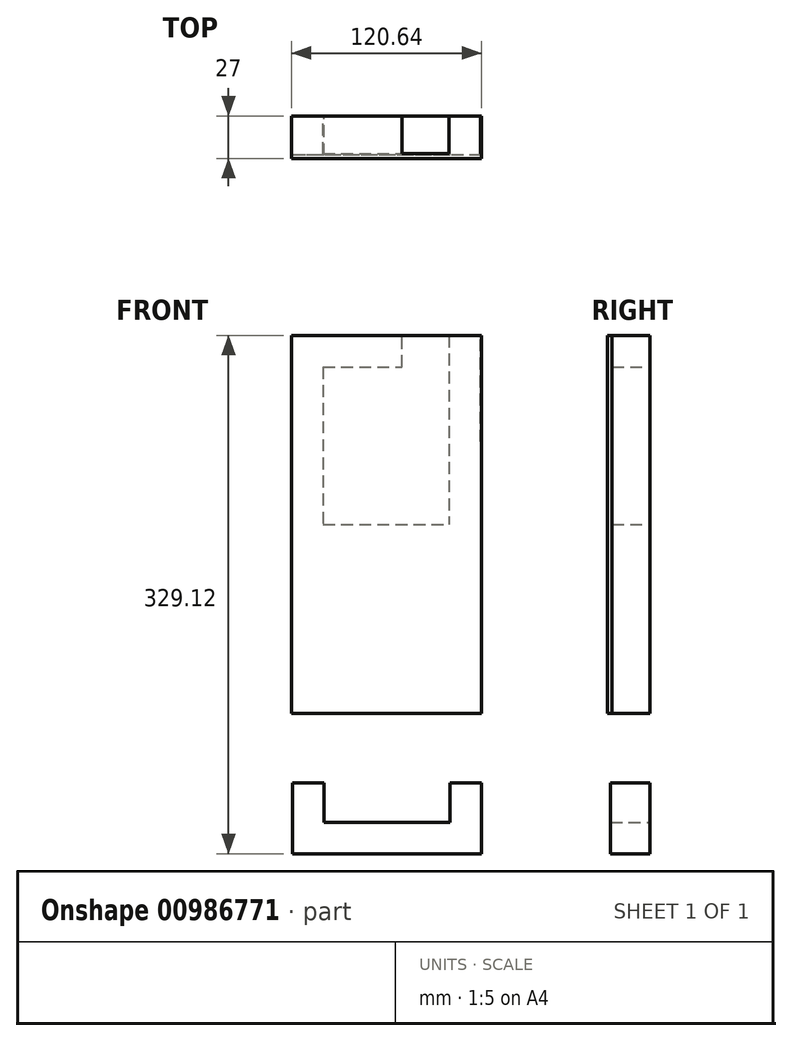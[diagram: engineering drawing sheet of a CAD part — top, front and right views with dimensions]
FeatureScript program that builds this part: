
annotation { "Feature Type Name" : "Feature", "Feature Type Description" : "" }
export const myFeature = defineFeature(function(context is Context, id is Id, definition is map)
    precondition{}
    {
        {
            var Q0;
            Q0=qCreatedBy(makeId("Front.planeOp"),FACE);
            var sketch = newSketch(context, id + "F0", { "sketchPlane" : qUnion([Q0])});
            skLineSegment(sketch, "E0.bottom", {"start": v(0, 0) * mm, "end": v(120, 0) * mm});
            skLineSegment(sketch, "E0.top", {"start": v(-0.64, 240) * mm, "end": v(119.36, 240) * mm});
            skLineSegment(sketch, "E0.left", {"start": v(0, 0) * mm, "end": v(-0.64, 240) * mm});
            skLineSegment(sketch, "E0.right", {"start": v(120, 0) * mm, "end": v(119.36, 240) * mm});
            skLineSegment(sketch, "E1.bottom", {"start": v(19.41, 220) * mm, "end": v(99.41, 220) * mm});
            skLineSegment(sketch, "E1.top", {"start": v(19.41, 40) * mm, "end": v(99.41, 40) * mm});
            skLineSegment(sketch, "E1.left", {"start": v(19.41, 200) * mm, "end": v(19.41, 40) * mm});
            skLineSegment(sketch, "E1.right", {"start": v(99.41, 220) * mm, "end": v(99.41, 40) * mm});
            skLineSegment(sketch, "E2.bottom", {"start": v(19.41, 120) * mm, "end": v(99.41, 120) * mm});
            skLineSegment(sketch, "E2.left", {"start": v(19.41, 120) * mm, "end": v(19.41, 220) * mm});
            skLineSegment(sketch, "E2.right", {"start": v(99.41, 120) * mm, "end": v(99.41, 130) * mm});
            skLineSegment(sketch, "E3", {"start": v(19.41, 220) * mm, "end": v(19.36, 240) * mm});
            skLineSegment(sketch, "E4", {"start": v(19.36, 240) * mm, "end": v(69.41, 240) * mm});
            skLineSegment(sketch, "E5", {"start": v(69.41, 240) * mm, "end": v(69.41, 220) * mm});
            skLineSegment(sketch, "E6", {"start": v(69.41, 220) * mm, "end": v(19.41, 220) * mm});
            skLineSegment(sketch, "E7.bottom", {"start": v(120, -44.12) * mm, "end": v(0, -44.12) * mm});
            skLineSegment(sketch, "E7.top", {"start": v(120, -89.12) * mm, "end": v(0, -89.12) * mm});
            skLineSegment(sketch, "E7.left", {"start": v(120, -44.12) * mm, "end": v(120, -89.12) * mm});
            skLineSegment(sketch, "E7.right", {"start": v(0, -44.12) * mm, "end": v(0, -89.12) * mm});
            skLineSegment(sketch, "E8.bottom", {"start": v(99.9, -44.12) * mm, "end": v(19.9, -44.12) * mm});
            skLineSegment(sketch, "E8.top", {"start": v(99.9, -69.12) * mm, "end": v(19.9, -69.12) * mm});
            skLineSegment(sketch, "E8.left", {"start": v(99.9, -44.12) * mm, "end": v(99.9, -69.12) * mm});
            skLineSegment(sketch, "E8.right", {"start": v(19.9, -44.12) * mm, "end": v(19.9, -69.12) * mm});
            skSolve(sketch);
        }
        {
            var Q0;
            {var subQ0=sQuery(id+"F0.wireOp",EDGE,"E3");var subQ8=makeQuery(id+"F0.imprint","IMPRINT",EDGE,{"derivedFrom":subQ0});var subQ27=makeQuery(id+"F0.imprint","IMPRINT",EDGE,{"derivedFrom":sQuery(id+"F0.wireOp",EDGE,"E8.top")});Q0=qUnion([makeQuery(id+"F0.imprint","IMPRINT",FACE,{"disambiguationData":[TD([[subQ27,-1.0]])]}),makeQuery(id+"F0.imprint","IMPRINT",FACE,{"disambiguationData":[TD([[makeQuery(id+"F0.imprint","IMPRINT",EDGE,{"derivedFrom":sQuery(id+"F0.wireOp",EDGE,"E7.top")}),-1.0]])]}),makeQuery(id+"F0.imprint","IMPRINT",FACE,{"disambiguationData":[TD([[makeQuery(id+"F0.imprint","IMPRINT",EDGE,{"derivedFrom":sQuery(id+"F0.wireOp",EDGE,"E0.bottom")}),1.0]])]}),makeQuery(id+"F0.imprint","IMPRINT",FACE,{"disambiguationData":[TD([[subQ8,-1.0]])]})]);}
            extrude(context, id + "F1", {"entities" : qUnion([Q0]), "depth" : 25 * mm, "offsetDistance" : 25 * mm});
        }
        {
            var Q0;
            {var subQ0=sQuery(id+"F0.wireOp",EDGE,"E1.top");Q0=makeQuery(id+"F0.imprint","IMPRINT",FACE,{"disambiguationData":[TD([[makeQuery(id+"F0.imprint","IMPRINT",EDGE,{"derivedFrom":subQ0}),1.0]])]});}
            extrude(context, id + "F2", {"entities" : qUnion([Q0]), "operationType" : NewBodyOperationType.ADD, "depth" : 25 * mm, "offsetDistance" : 25 * mm});
        }
        {
            var Q0;
            {var subQ0=sQuery(id+"F0.wireOp",EDGE,"E1.right");var subQ1=sQuery(id+"F0.wireOp",EDGE,"E1.left");var subQ2=sQuery(id+"F0.wireOp",EDGE,"E1.top");Q0=makeQuery(id+"F2.boolean.opBoolean","MERGE",FACE,{"derivedFrom":[makeQuery(id+"F1.opExtrude","CAP_FACE",FACE,{"disambiguationData":[OSD([sQuery(id+"F0.wireOp",EDGE,"E0.bottom"),sQuery(id+"F0.wireOp",EDGE,"E0.top"),sQuery(id+"F0.wireOp",EDGE,"E0.left"),sQuery(id+"F0.wireOp",EDGE,"E0.right"),sQuery(id+"F0.wireOp",EDGE,"E1.bottom"),subQ2,subQ1,subQ0,sQuery(id+"F0.wireOp",EDGE,"E2.left")])],"isStart":false}),makeQuery(id+"F2.opExtrude","CAP_FACE",FACE,{"disambiguationData":[OSD([subQ2,subQ1,subQ0,sQuery(id+"F0.wireOp",EDGE,"E2.bottom")])],"isStart":false})]});}
            var sketch = newSketch(context, id + "F3", { "sketchPlane" : qUnion([Q0])});
            skLineSegment(sketch, "E9.bottom", {"start": v(19.62, 240) * mm, "end": v(99.41, 240) * mm});
            skLineSegment(sketch, "E9.top", {"start": v(19.62, 220) * mm, "end": v(99.41, 220) * mm});
            skLineSegment(sketch, "E9.left", {"start": v(19.62, 240) * mm, "end": v(19.62, 220) * mm});
            skLineSegment(sketch, "E9.right", {"start": v(99.41, 240) * mm, "end": v(99.41, 220) * mm});
            skSolve(sketch);
        }
        {
            var Q0;
            Q0=makeQuery(id+"F3.imprint","IMPRINT",FACE,{"disambiguationData":[TD([[makeQuery(id+"F3.imprint","IMPRINT",EDGE,{"derivedFrom":sQuery(id+"F3.wireOp",EDGE,"E9.bottom")}),-1.0]])]});
            extrude(context, id + "F4", {"entities" : qUnion([Q0]), "operationType" : NewBodyOperationType.REMOVE, "oppositeDirection" : true, "depth" : 25 * mm, "offsetDistance" : 25 * mm});
        }
        {
            var Q0;
            {var subQ0=sQuery(id+"F0.wireOp",EDGE,"E1.right");var subQ1=sQuery(id+"F0.wireOp",EDGE,"E1.left");var subQ2=sQuery(id+"F0.wireOp",EDGE,"E1.top");Q0=makeQuery(id+"F2.boolean.opBoolean","MERGE",FACE,{"derivedFrom":[makeQuery(id+"F1.opExtrude","CAP_FACE",FACE,{"disambiguationData":[OSD([sQuery(id+"F0.wireOp",EDGE,"E0.bottom"),sQuery(id+"F0.wireOp",EDGE,"E0.top"),sQuery(id+"F0.wireOp",EDGE,"E0.left"),sQuery(id+"F0.wireOp",EDGE,"E0.right"),sQuery(id+"F0.wireOp",EDGE,"E1.bottom"),subQ2,subQ1,subQ0,sQuery(id+"F0.wireOp",EDGE,"E2.left")])],"isStart":false}),makeQuery(id+"F2.opExtrude","CAP_FACE",FACE,{"disambiguationData":[OSD([subQ2,subQ1,subQ0,sQuery(id+"F0.wireOp",EDGE,"E2.bottom")])],"isStart":false})]});}
            var sketch = newSketch(context, id + "F5", { "sketchPlane" : qUnion([Q0])});
            skLineSegment(sketch, "E10.bottom", {"start": v(-0.64, 240) * mm, "end": v(119.36, 240) * mm});
            skLineSegment(sketch, "E10.top", {"start": v(-0.64, 240) * mm, "end": v(119.36, 240) * mm});
            skLineSegment(sketch, "E10.left", {"start": v(-0.64, 240) * mm, "end": v(-0.64, 240) * mm});
            skLineSegment(sketch, "E10.right", {"start": v(119.36, 240) * mm, "end": v(119.36, 240) * mm});
            skLineSegment(sketch, "E11.bottom", {"start": v(120, 0) * mm, "end": v(0, 0) * mm});
            skLineSegment(sketch, "E11.top", {"start": v(120, 0) * mm, "end": v(0, 0) * mm});
            skLineSegment(sketch, "E11.left", {"start": v(120, 0) * mm, "end": v(120, 0) * mm});
            skLineSegment(sketch, "E11.right", {"start": v(0, 0) * mm, "end": v(0, 0) * mm});
            skLineSegment(sketch, "E12.bottom", {"start": v(-0.64, 240) * mm, "end": v(120, 240) * mm});
            skLineSegment(sketch, "E12.top", {"start": v(-0.64, 0) * mm, "end": v(120, 0) * mm});
            skLineSegment(sketch, "E12.left", {"start": v(-0.64, 240) * mm, "end": v(-0.64, 0) * mm});
            skLineSegment(sketch, "E12.right", {"start": v(120, 240) * mm, "end": v(120, 0) * mm});
            skSolve(sketch);
        }
        {
            var Q0;
            Q0=makeQuery(id+"F5.imprint","IMPRINT",FACE,{"disambiguationData":[TD([[makeQuery(id+"F5.imprint","IMPRINT",EDGE,{"derivedFrom":sQuery(id+"F5.wireOp",EDGE,"E12.top")}),1.0]])]});
            var Q1;
            Q1 = qSketchRegion(id + "F5", true);
            extrude(context, id + "F6", {"entities" : qUnion([Q0, Q1]), "operationType" : NewBodyOperationType.ADD, "oppositeDirection" : true, "depth" : 1 * mm, "offsetDistance" : 25 * mm, "hasSecondDirection" : true, "secondDirectionOppositeDirection" : false, "secondDirectionDepth" : 2 * mm});
        }
        {
            var Q0;
            {var subQ0=sQuery(id+"F0.wireOp",EDGE,"E3");Q0=makeQuery(id+"F0.imprint","IMPRINT",FACE,{"disambiguationData":[TD([[makeQuery(id+"F0.imprint","IMPRINT",EDGE,{"derivedFrom":subQ0}),-1.0]])]});}
            extrude(context, id + "F7", {"entities" : qUnion([Q0]), "operationType" : NewBodyOperationType.ADD, "depth" : 25 * mm, "offsetDistance" : 25 * mm});
        }
        {
            var Q0;
            Q0=makeQuery(id+"F0.imprint","IMPRINT",FACE,{"disambiguationData":[TD([[makeQuery(id+"F0.imprint","IMPRINT",EDGE,{"derivedFrom":sQuery(id+"F0.wireOp",EDGE,"E8.top")}),-1.0]])]});
            extrude(context, id + "F8", {"entities" : qUnion([Q0]), "operationType" : NewBodyOperationType.REMOVE, "oppositeDirection" : true, "depth" : 25 * mm, "offsetDistance" : 25 * mm});
        }
        {
            var Q0;
            Q0=makeQuery(id+"F0.imprint","IMPRINT",FACE,{"disambiguationData":[TD([[makeQuery(id+"F0.imprint","IMPRINT",EDGE,{"derivedFrom":sQuery(id+"F0.wireOp",EDGE,"E8.top")}),-1.0]])]});
            extrude(context, id + "F9", {"entities" : qUnion([Q0]), "operationType" : NewBodyOperationType.REMOVE, "oppositeDirection" : true, "depth" : -25 * mm, "offsetDistance" : 25 * mm});
        }
    });
